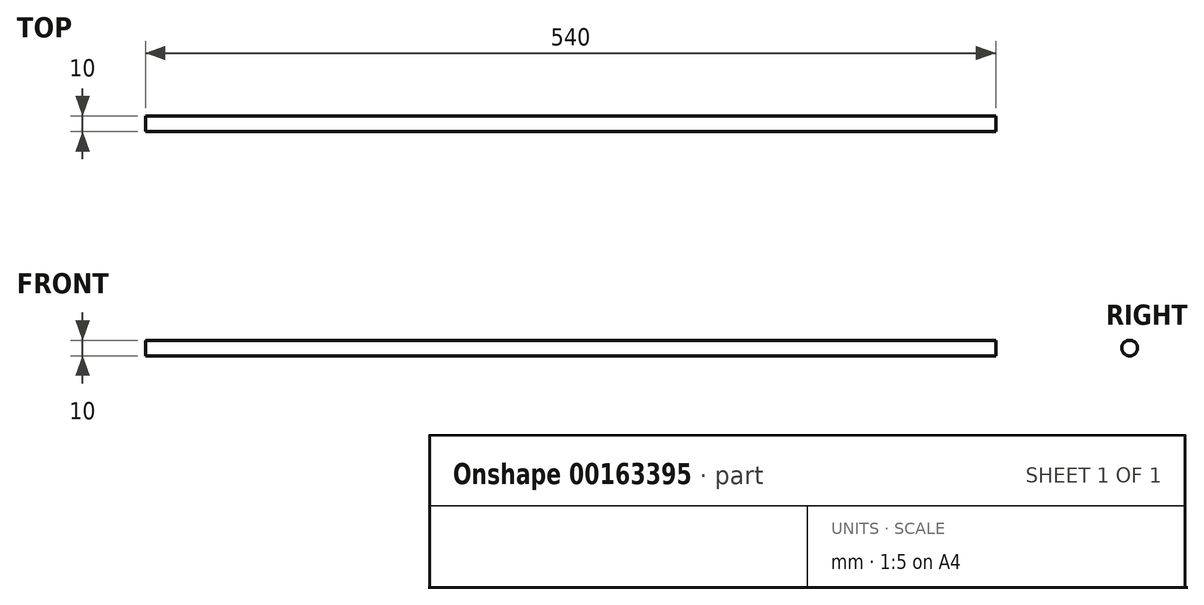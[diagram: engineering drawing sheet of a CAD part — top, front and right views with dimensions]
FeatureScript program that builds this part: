
annotation { "Feature Type Name" : "Feature", "Feature Type Description" : "" }
export const myFeature = defineFeature(function(context is Context, id is Id, definition is map)
    precondition{}
    {
        {
            var Q0;
            Q0=qCreatedBy(makeId("Right.planeOp"),FACE);
            var sketch = newSketch(context, id + "F0", { "sketchPlane" : qUnion([Q0])});
            skCircle(sketch, "E0", {"center": v(0, 0) * mm, "radius": 5 * mm});
            skSolve(sketch);
        }
        {
            var Q0;
            Q0=makeQuery(id+"F0.imprint","IMPRINT",FACE,{"disambiguationData":[TD([[makeQuery(id+"F0.imprint","IMPRINT",EDGE,{"derivedFrom":sQuery(id+"F0.wireOp",EDGE,"E0")}),1.0]])]});
            var Q1;
            Q1=sQuery(id+"F0.wireOp",EDGE,"E0");
            extrude(context, id + "F1", {"entities" : qUnion([Q0]), "surfaceEntities" : qUnion([Q1]), "endBound" : BoundingType.SYMMETRIC, "depth" : 540 * mm});
        }
    });
